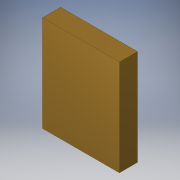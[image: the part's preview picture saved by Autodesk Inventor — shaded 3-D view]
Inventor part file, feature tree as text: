
AUTODESK INVENTOR PART (.ipt)
format: ipt  version: 2017 (Build 210142000, 142)  size: 90,624 bytes
history: native  units: in
note: dims shown in document units (in); Inventor stores cm internally (conversion verified against a paired STEP export)
features: extrude x1, sketch x1
ambient origin geometry x8: Origin, YZ Plane, XZ Plane, XY Plane, X Axis, Y Axis, Z Axis, Center Point
bodies: Solid1 (feature_tree)
feature tree (2):
  extrude  "Extrusion1"  Depth=10.0in
  sketch  "Sketch1"  dims[d0=8.0in d1=10.0in d2=1.88in d3=0.0in]
